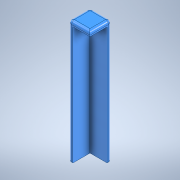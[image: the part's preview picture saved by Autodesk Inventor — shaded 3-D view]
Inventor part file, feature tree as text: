
AUTODESK INVENTOR PART (.ipt)
format: ipt  version: 2021 (Build 250183000, 183)  size: 135,168 bytes
history: native  units: mm
features: extrude x3, sketch x2, other x1, fillet x1
ambient origin geometry x8: Origin, YZ Plane, XZ Plane, XY Plane, X Axis, Y Axis, Z Axis, Center Point
bodies: Solid1 (feature_tree)
feature tree (7):
  other  "DoosjeHoeken"
  extrude  "Extrusion1"  Depth=15.0mm
  extrude  "Extrusion3"  Depth=3.0mm
  extrude  "Extrusion4"  Depth=12.0mm
  fillet  "Fillet3"  Radius=12.0mm
  sketch  "Sketch4"  dims[d0=15.0mm d1=15.0mm]
  sketch  "Sketch6"  dims[d2=86.0mm d3=0.0mm d10=3.0mm d11=12.0mm d12=12.0mm d13=3.0mm d14=3.0mm d15=0.0mm d16=12.0mm d17=0.0mm d18=2.0mm]
